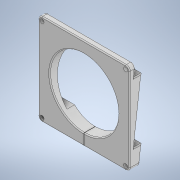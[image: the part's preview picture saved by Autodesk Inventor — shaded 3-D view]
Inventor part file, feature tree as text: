
AUTODESK INVENTOR PART (.ipt)
format: ipt  version: 2022.1 (Build 261234020, 234B)  size: 246,272 bytes
history: native  units: in
note: dims shown in document units (in); Inventor stores cm internally (conversion verified against a paired STEP export)
features: fillet x4, extrude x3, sketch x2, hole x1
ambient origin geometry x8: Origin, YZ Plane, XZ Plane, XY Plane, X Axis, Y Axis, Z Axis, Center Point
bodies: Solid2 (feature_tree)
feature tree (10):
  extrude  "Extrusion3"  Depth=4.0in
  sketch  "Sketch5"  dims[d30=4.0in d31=0.5in d32=4.0in d33=6.0in d34=0.4in d35=0.75in d36=6.0in d37=0.0in d38=0.25in d39=0.25in d40=4.5in d41=0.0in d42=0.0in d43=0.266in d44=0.75in d45=0.625in d46=0.19in d47=0.5635in d48=1.0in d49=0.8108in d50=0.25in d51=0.01in d52=0.0in d53=0.0in d54=0.0625in d55=0.0625in d56=0.0625in]
  extrude  "Extrusion4"  Depth=0.0625in
  hole  "Hole2"  [1 undecoded]
  fillet  "Fillet2"  Radius=6.0in
  extrude  "Extrusion5"  Depth=0.0625in
  fillet  "Fillet3"  Radius=0.75in
  fillet  "Fillet4"  Radius=6.0in
  fillet  "Fillet5"  [1 undecoded]
  sketch  "Sketch4"  dims[d28=0.5in d29=4.0in]
note: 2 required parameter values undecoded (feature->parameter linkage not recoverable at this tier; creation-order binding heuristic only, values carry confidence <= 0.55)
